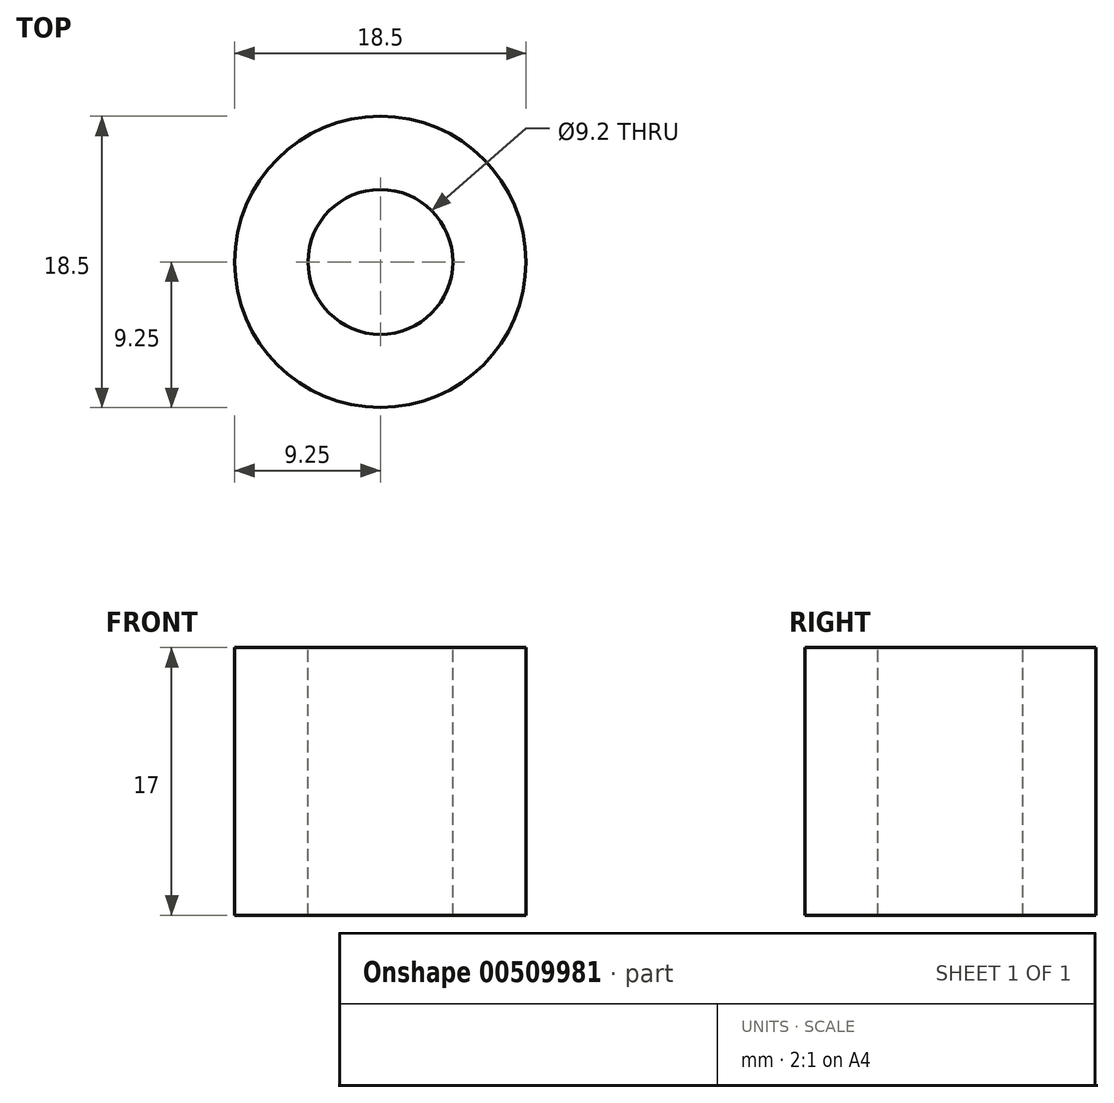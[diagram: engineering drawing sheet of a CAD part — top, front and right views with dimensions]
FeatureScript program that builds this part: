
annotation { "Feature Type Name" : "Feature", "Feature Type Description" : "" }
export const myFeature = defineFeature(function(context is Context, id is Id, definition is map)
    precondition{}
    {
        {
            var Q0;
            Q0=qCreatedBy(makeId("Top.planeOp"),FACE);
            var sketch = newSketch(context, id + "F0", { "sketchPlane" : qUnion([Q0])});
            skCircle(sketch, "E0", {"center": v(0, 0) * mm, "radius": 4.6 * mm});
            skCircle(sketch, "E1", {"center": v(0, 0) * mm, "radius": 15 * mm});
            skCircle(sketch, "E2", {"center": v(0, 0) * mm, "radius": 9.25 * mm});
            skSolve(sketch);
        }
        {
            var Q0;
            Q0=makeQuery(id+"F0.imprint","IMPRINT",FACE,{"disambiguationData":[TD([[makeQuery(id+"F0.imprint","IMPRINT",EDGE,{"derivedFrom":sQuery(id+"F0.wireOp",EDGE,"E0")}),-1.0]])]});
            extrude(context, id + "F1", {"entities" : qUnion([Q0]), "depth" : -17 * mm});
        }
    });
